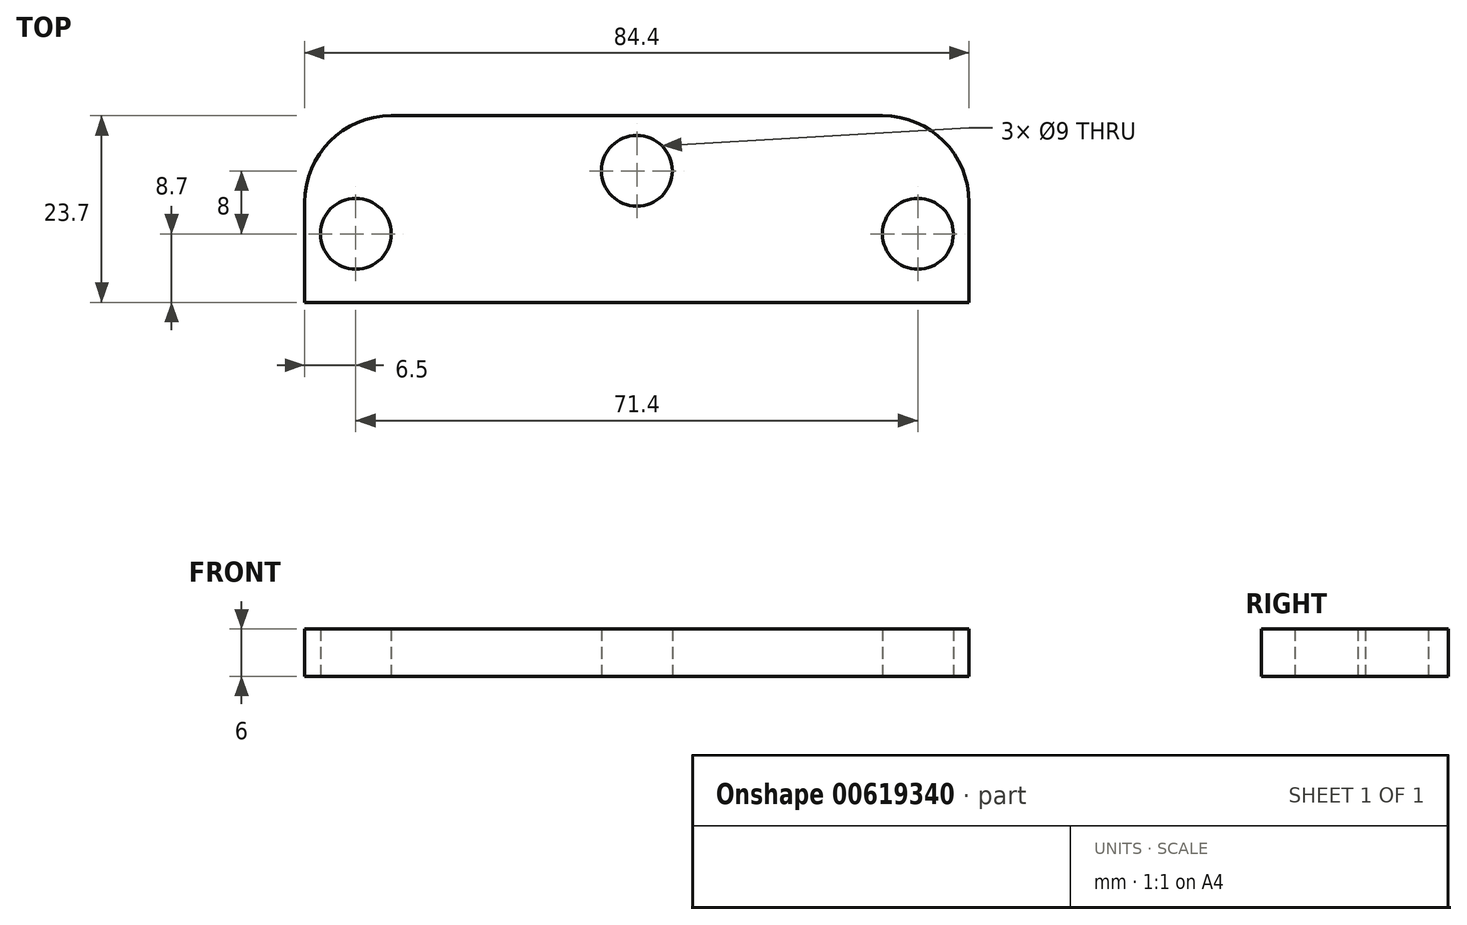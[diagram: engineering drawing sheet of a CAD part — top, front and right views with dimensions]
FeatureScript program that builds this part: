
annotation { "Feature Type Name" : "Feature", "Feature Type Description" : "" }
export const myFeature = defineFeature(function(context is Context, id is Id, definition is map)
    precondition{}
    {
        {
            var Q0;
            Q0=qCreatedBy(makeId("Top.planeOp"),FACE);
            var sketch = newSketch(context, id + "F0", { "sketchPlane" : qUnion([Q0])});
            skLineSegment(sketch, "E0.bottom", {"start": v(-44.2, 0) * mm, "end": v(44.2, 0) * mm, "construction": true});
            skLineSegment(sketch, "E0.top", {"start": v(-31.2, 27.7) * mm, "end": v(31.2, 27.7) * mm, "construction": true});
            skLineSegment(sketch, "E0.left", {"start": v(-44.2, 0) * mm, "end": v(-44.2, 14.7) * mm, "construction": true});
            skLineSegment(sketch, "E0.right", {"start": v(44.2, 0) * mm, "end": v(44.2, 14.7) * mm, "construction": true});
            skPoint(sketch, "E1", {"position": v(0, 0) * mm});
            skPoint(sketch, "E2.visualSharp", {"position": v(-44.2, 27.7) * mm});
            skArc(sketch, "E2.filletArc", {"start": v(-31.2, 27.7) * mm, "mid": v(-40.4, 23.9) * mm, "end": v(-44.2, 14.7) * mm, "construction": true});
            skPoint(sketch, "E3.visualSharp", {"position": v(44.2, 27.7) * mm});
            skArc(sketch, "E3.filletArc", {"start": v(44.2, 14.7) * mm, "mid": v(40.4, 23.9) * mm, "end": v(31.2, 27.7) * mm, "construction": true});
            skCircle(sketch, "E4", {"center": v(0, 18.7) * mm, "radius": 4.5 * mm});
            skCircle(sketch, "E5", {"center": v(35.7, 10.7) * mm, "radius": 4.5 * mm});
            skCircle(sketch, "E6", {"center": v(-35.7, 10.7) * mm, "radius": 4.5 * mm});
            skArc(sketch, "E7.0", {"start": v(-31.2, 25.7) * mm, "mid": v(-38.98, 22.48) * mm, "end": v(-42.2, 14.7) * mm});
            skArc(sketch, "E7.1", {"start": v(42.2, 14.7) * mm, "mid": v(38.98, 22.48) * mm, "end": v(31.2, 25.7) * mm});
            skLineSegment(sketch, "E7.2", {"start": v(42.2, 2) * mm, "end": v(42.2, 14.7) * mm});
            skLineSegment(sketch, "E7.3", {"start": v(-31.2, 25.7) * mm, "end": v(31.2, 25.7) * mm});
            skLineSegment(sketch, "E7.4", {"start": v(-42.2, 2) * mm, "end": v(42.2, 2) * mm});
            skLineSegment(sketch, "E7.5", {"start": v(-42.2, 2) * mm, "end": v(-42.2, 14.7) * mm});
            skSolve(sketch);
        }
        {
            var Q0;
            Q0=makeQuery(id+"F0.imprint","IMPRINT",FACE,{"disambiguationData":[TD([[makeQuery(id+"F0.imprint","IMPRINT",EDGE,{"derivedFrom":sQuery(id+"F0.wireOp",EDGE,"E4")}),-1.0]])]});
            extrude(context, id + "F1", {"entities" : qUnion([Q0]), "depth" : 6 * mm, "offsetDistance" : 25 * mm});
        }
    });
